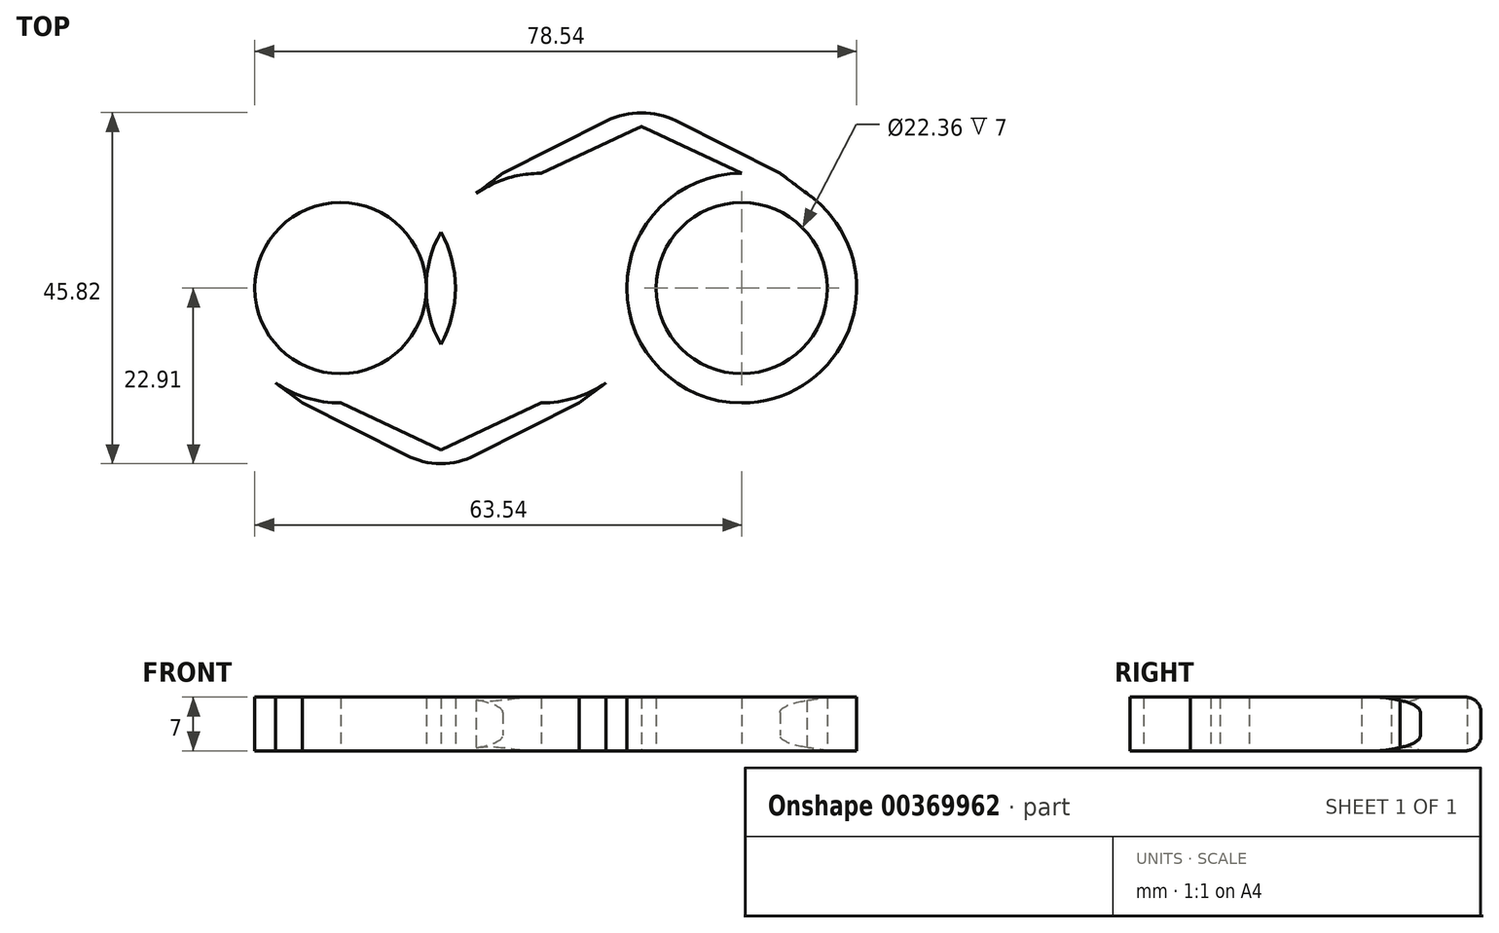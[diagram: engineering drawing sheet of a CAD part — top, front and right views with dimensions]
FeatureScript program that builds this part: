
annotation { "Feature Type Name" : "Feature", "Feature Type Description" : "" }
export const myFeature = defineFeature(function(context is Context, id is Id, definition is map)
    precondition{}
    {
        {
            var Q0;
            Q0=qCreatedBy(makeId("Top.planeOp"),FACE);
            var sketch = newSketch(context, id + "F0", { "sketchPlane" : qUnion([Q0])});
            skCircle(sketch, "E0", {"center": v(0, 0) * mm, "radius": 11.18 * mm});
            skCircle(sketch, "E1", {"center": v(0, 0) * mm, "radius": 15 * mm});
            skCircle(sketch, "E2", {"center": v(-26.18, 0) * mm, "radius": 11.18 * mm});
            skCircle(sketch, "E3", {"center": v(-26.18, 0) * mm, "radius": 15 * mm});
            skLineSegment(sketch, "E4", {"start": v(-26.18, 0) * mm, "end": v(0, 0) * mm, "construction": true});
            skLineSegment(sketch, "E5", {"start": v(-26.18, 0) * mm, "end": v(-26.18, 2) * mm, "construction": true});
            skLineSegment(sketch, "E6", {"start": v(-26.18, 0) * mm, "end": v(-26.18, -2) * mm, "construction": true});
            skLineSegment(sketch, "E7", {"start": v(0, 0) * mm, "end": v(0, 2) * mm, "construction": true});
            skLineSegment(sketch, "E8", {"start": v(0, 0) * mm, "end": v(0, -2) * mm, "construction": true});
            skLineSegment(sketch, "E9", {"start": v(-14.87, 2) * mm, "end": v(-11.3, 2) * mm});
            skLineSegment(sketch, "E10", {"start": v(-14.87, -2) * mm, "end": v(-11.3, -2) * mm});
            skLineSegment(sketch, "E11", {"start": v(-11.3, 2) * mm, "end": v(-26.18, 2) * mm, "construction": true});
            skLineSegment(sketch, "E12", {"start": v(-26.18, -2) * mm, "end": v(-11.3, -2) * mm, "construction": true});
            skLineSegment(sketch, "E13", {"start": v(-14.87, 2) * mm, "end": v(0, 2) * mm, "construction": true});
            skLineSegment(sketch, "E14", {"start": v(-14.87, -2) * mm, "end": v(0, -2) * mm, "construction": true});
            skLineSegment(sketch, "E15", {"start": v(-26.17, -2) * mm, "end": v(-26.17, -15) * mm, "construction": true});
            skLineSegment(sketch, "E16", {"start": v(0, -2) * mm, "end": v(0, -15) * mm, "construction": true});
            skLineSegment(sketch, "E17.MirrorCS", {"start": v(26.18, 0) * mm, "end": v(26.18, 2) * mm, "construction": true});
            skLineSegment(sketch, "E18.MirrorCS", {"start": v(26.18, 0) * mm, "end": v(26.18, -2) * mm, "construction": true});
            skLineSegment(sketch, "E19.MirrorCS", {"start": v(14.87, 2) * mm, "end": v(11.3, 2) * mm});
            skLineSegment(sketch, "E20.MirrorCS", {"start": v(14.87, -2) * mm, "end": v(11.3, -2) * mm});
            skLineSegment(sketch, "E21.MirrorCS", {"start": v(14.87, -2) * mm, "end": v(0, -2) * mm, "construction": true});
            skLineSegment(sketch, "E22.MirrorCS", {"start": v(26.18, -2) * mm, "end": v(26.18, -15) * mm, "construction": true});
            skCircle(sketch, "E23.MirrorC", {"center": v(26.18, 0) * mm, "radius": 15 * mm});
            skLineSegment(sketch, "E24.MirrorCS", {"start": v(26.18, 0) * mm, "end": v(0, 0) * mm, "construction": true});
            skLineSegment(sketch, "E25.MirrorCS", {"start": v(26.18, -2) * mm, "end": v(11.3, -2) * mm, "construction": true});
            skLineSegment(sketch, "E26.MirrorCS", {"start": v(11.3, 2) * mm, "end": v(26.18, 2) * mm, "construction": true});
            skCircle(sketch, "E27.MirrorC", {"center": v(26.18, 0) * mm, "radius": 11.18 * mm});
            skLineSegment(sketch, "E28.MirrorCS", {"start": v(14.87, 2) * mm, "end": v(0, 2) * mm, "construction": true});
            skLineSegment(sketch, "E29.MirrorCS", {"start": v(0, 2) * mm, "end": v(0, 15) * mm, "construction": true});
            skLineSegment(sketch, "E30.MirrorCS", {"start": v(-26.18, 2) * mm, "end": v(-11.3, 2) * mm, "construction": true});
            skLineSegment(sketch, "E31.MirrorCS", {"start": v(11.3, -2) * mm, "end": v(26.18, -2) * mm, "construction": true});
            skLineSegment(sketch, "E32.MirrorCS", {"start": v(-26.17, 2) * mm, "end": v(-26.18, 15) * mm, "construction": true});
            skLineSegment(sketch, "E33.MirrorCS", {"start": v(-11.3, -2) * mm, "end": v(-26.18, -2) * mm, "construction": true});
            skLineSegment(sketch, "E34.MirrorCS", {"start": v(26.18, 2) * mm, "end": v(11.3, 2) * mm, "construction": true});
            skLineSegment(sketch, "E35.MirrorCS", {"start": v(26.18, 2) * mm, "end": v(26.18, 15) * mm, "construction": true});
            skLineSegment(sketch, "E36", {"start": v(-26.17, -15) * mm, "end": v(0, -15) * mm, "construction": true});
            skPoint(sketch, "E37.endSnap0", {"position": v(-13.09, -2) * mm});
            skLineSegment(sketch, "E38", {"start": v(-26.17, -15) * mm, "end": v(-31.17, -15) * mm});
            skLineSegment(sketch, "E39", {"start": v(0, -15) * mm, "end": v(5, -15) * mm});
            skLineSegment(sketch, "E40", {"start": v(0, -15) * mm, "end": v(-13.09, -21.1) * mm});
            skLineSegment(sketch, "E41", {"start": v(-26.17, -15) * mm, "end": v(-13.09, -21.1) * mm});
            skLineSegment(sketch, "E42", {"start": v(-13.09, -21.1) * mm, "end": v(-13.09, -24.1) * mm});
            skLineSegment(sketch, "E43", {"start": v(-31.17, -15) * mm, "end": v(-13.09, -24.1) * mm});
            skLineSegment(sketch, "E44", {"start": v(-13.09, -24.1) * mm, "end": v(5, -15) * mm});
            skLineSegment(sketch, "E45", {"start": v(5, -15) * mm, "end": v(8.55, -12.32) * mm});
            skLineSegment(sketch, "E46", {"start": v(-31.17, -15) * mm, "end": v(-34.73, -12.32) * mm});
            skLineSegment(sketch, "E47.MirrorCS", {"start": v(-5, -15) * mm, "end": v(-8.55, -12.32) * mm});
            skLineSegment(sketch, "E48.MirrorCS", {"start": v(31.17, -15) * mm, "end": v(13.09, -24.1) * mm});
            skLineSegment(sketch, "E49.MirrorCS", {"start": v(0, -15) * mm, "end": v(13.09, -21.1) * mm});
            skLineSegment(sketch, "E50.MirrorCS", {"start": v(26.17, -15) * mm, "end": v(13.09, -21.1) * mm});
            skLineSegment(sketch, "E51.MirrorCS", {"start": v(26.17, -15) * mm, "end": v(31.17, -15) * mm});
            skLineSegment(sketch, "E52.MirrorCS", {"start": v(31.17, -15) * mm, "end": v(34.73, -12.32) * mm});
            skLineSegment(sketch, "E53.MirrorCS", {"start": v(0, -15) * mm, "end": v(-5, -15) * mm});
            skLineSegment(sketch, "E54.MirrorCS", {"start": v(13.09, -21.1) * mm, "end": v(13.09, -24.1) * mm});
            skLineSegment(sketch, "E55.MirrorCS", {"start": v(13.09, -24.1) * mm, "end": v(-5, -15) * mm});
            skLineSegment(sketch, "E56.MirrorCS", {"start": v(26.17, -15) * mm, "end": v(0, -15) * mm, "construction": true});
            skLineSegment(sketch, "E57.MirrorCS", {"start": v(0, 15) * mm, "end": v(-5, 15) * mm});
            skLineSegment(sketch, "E58.MirrorCS", {"start": v(0, 15) * mm, "end": v(5, 15) * mm});
            skLineSegment(sketch, "E59.MirrorCS", {"start": v(-26.17, 15) * mm, "end": v(-31.17, 15) * mm});
            skLineSegment(sketch, "E60.MirrorCS", {"start": v(13.09, 21.1) * mm, "end": v(13.09, 24.1) * mm});
            skLineSegment(sketch, "E61.MirrorCS", {"start": v(5, 15) * mm, "end": v(8.55, 12.32) * mm});
            skLineSegment(sketch, "E62.MirrorCS", {"start": v(-13.09, 24.1) * mm, "end": v(5, 15) * mm});
            skLineSegment(sketch, "E63.MirrorCS", {"start": v(-13.09, 21.1) * mm, "end": v(-13.09, 24.1) * mm});
            skLineSegment(sketch, "E64.MirrorCS", {"start": v(26.17, 15) * mm, "end": v(31.17, 15) * mm});
            skLineSegment(sketch, "E65.MirrorCS", {"start": v(31.17, 15) * mm, "end": v(13.09, 24.1) * mm});
            skLineSegment(sketch, "E66.MirrorCS", {"start": v(-31.17, 15) * mm, "end": v(-13.09, 24.1) * mm});
            skLineSegment(sketch, "E67.MirrorCS", {"start": v(26.17, 15) * mm, "end": v(0, 15) * mm, "construction": true});
            skLineSegment(sketch, "E68.MirrorCS", {"start": v(0, 15) * mm, "end": v(-13.09, 21.1) * mm});
            skLineSegment(sketch, "E69.MirrorCS", {"start": v(0, 15) * mm, "end": v(13.09, 21.1) * mm});
            skLineSegment(sketch, "E70.MirrorCS", {"start": v(-5, 15) * mm, "end": v(-8.55, 12.32) * mm});
            skLineSegment(sketch, "E71.MirrorCS", {"start": v(-26.17, 15) * mm, "end": v(0, 15) * mm, "construction": true});
            skLineSegment(sketch, "E72.MirrorCS", {"start": v(-26.17, 15) * mm, "end": v(-13.09, 21.1) * mm});
            skLineSegment(sketch, "E73.MirrorCS", {"start": v(26.17, 15) * mm, "end": v(13.09, 21.1) * mm});
            skLineSegment(sketch, "E74.MirrorCS", {"start": v(13.09, 24.1) * mm, "end": v(-5, 15) * mm});
            skLineSegment(sketch, "E75.MirrorCS", {"start": v(-31.17, 15) * mm, "end": v(-34.73, 12.32) * mm});
            skLineSegment(sketch, "E76.MirrorCS", {"start": v(31.17, 15) * mm, "end": v(34.73, 12.32) * mm});
            skSolve(sketch);
        }
        {
            var Q0;
            {var subQ8=sQuery(id+"F0.wireOp",EDGE,"E2");Q0=makeQuery(id+"F0.imprint","IMPRINT",FACE,{"disambiguationData":[TD([[makeQuery(id+"F0.imprint","IMPRINT",EDGE,{"derivedFrom":subQ8}),1.0]])]});}
            var Q1;
            {var subQ6=sQuery(id+"F0.wireOp",EDGE,"E27.MirrorC");Q1=makeQuery(id+"F0.imprint","IMPRINT",FACE,{"disambiguationData":[TD([[makeQuery(id+"F0.imprint","IMPRINT",EDGE,{"derivedFrom":subQ6}),-1.0]])]});}
            var Q2;
            {var subQ4=sQuery(id+"F0.wireOp",EDGE,"E3");var subQ5=makeQuery(id+"F0.imprint","INTERSECT",VERTEX,{"derivedFrom":[sQuery(id+"F0.wireOp",EDGE,"E9"),subQ4]});Q2=makeQuery(id+"F0.imprint","IMPRINT",FACE,{"disambiguationData":[TD([[makeQuery(id+"F0.imprint","IMPRINT",EDGE,{"disambiguationData":[TD([[subQ5,1.0]])],"derivedFrom":subQ4}),1.0]])]});}
            var Q3;
            {var subQ0=sQuery(id+"F0.wireOp",EDGE,"E42");Q3=makeQuery(id+"F0.imprint","IMPRINT",FACE,{"disambiguationData":[TD([[makeQuery(id+"F0.imprint","IMPRINT",EDGE,{"derivedFrom":subQ0}),1.0]])]});}
            var Q4;
            {var subQ1=sQuery(id+"F0.wireOp",EDGE,"E20.MirrorCS");Q4=makeQuery(id+"F0.imprint","IMPRINT",FACE,{"disambiguationData":[TD([[makeQuery(id+"F0.imprint","IMPRINT",EDGE,{"derivedFrom":subQ1}),-1.0]])]});}
            var Q5;
            {var subQ0=sQuery(id+"F0.wireOp",EDGE,"E10");Q5=makeQuery(id+"F0.imprint","IMPRINT",FACE,{"disambiguationData":[TD([[makeQuery(id+"F0.imprint","IMPRINT",EDGE,{"derivedFrom":subQ0}),-1.0]])]});}
            var Q6;
            {var subQ0=sQuery(id+"F0.wireOp",EDGE,"E9");Q6=makeQuery(id+"F0.imprint","IMPRINT",FACE,{"disambiguationData":[TD([[makeQuery(id+"F0.imprint","IMPRINT",EDGE,{"derivedFrom":subQ0}),1.0]])]});}
            var Q7;
            {var subQ0=sQuery(id+"F0.wireOp",EDGE,"E74.MirrorCS");var subQ1=sQuery(id+"F0.wireOp",EDGE,"E62.MirrorCS");var subQ2=makeQuery(id+"F0.imprint","INTERSECT",VERTEX,{"derivedFrom":[subQ1,subQ0]});Q7=makeQuery(id+"F0.imprint","IMPRINT",FACE,{"disambiguationData":[TD([[makeQuery(id+"F0.imprint","IMPRINT",EDGE,{"disambiguationData":[TD([[subQ2,-1.0]])],"derivedFrom":subQ1}),-1.0]])]});}
            var Q8;
            {var subQ3=sQuery(id+"F0.wireOp",EDGE,"E55.MirrorCS");var subQ5=sQuery(id+"F0.wireOp",EDGE,"E44");var subQ6=makeQuery(id+"F0.imprint","INTERSECT",VERTEX,{"derivedFrom":[subQ5,subQ3]});Q8=makeQuery(id+"F0.imprint","IMPRINT",FACE,{"disambiguationData":[TD([[makeQuery(id+"F0.imprint","IMPRINT",EDGE,{"disambiguationData":[TD([[subQ6,-1.0]])],"derivedFrom":subQ5}),1.0]])]});}
            var Q9;
            {var subQ0=sQuery(id+"F0.wireOp",EDGE,"E57.MirrorCS");Q9=makeQuery(id+"F0.imprint","IMPRINT",FACE,{"disambiguationData":[TD([[makeQuery(id+"F0.imprint","IMPRINT",EDGE,{"derivedFrom":subQ0}),-1.0]])]});}
            var Q10;
            Q10=makeQuery(id+"F0.imprint","IMPRINT",FACE,{"disambiguationData":[TD([[makeQuery(id+"F0.imprint","IMPRINT",EDGE,{"derivedFrom":sQuery(id+"F0.wireOp",EDGE,"E38")}),1.0]])]});
            var Q11;
            {var subQ4=sQuery(id+"F0.wireOp",EDGE,"E3");var subQ5=makeQuery(id+"F0.imprint","INTERSECT",VERTEX,{"derivedFrom":[sQuery(id+"F0.wireOp",EDGE,"E10"),subQ4]});Q11=makeQuery(id+"F0.imprint","IMPRINT",FACE,{"disambiguationData":[TD([[makeQuery(id+"F0.imprint","IMPRINT",EDGE,{"disambiguationData":[TD([[subQ5,1.0]])],"derivedFrom":subQ4}),1.0]])]});}
            var Q12;
            {var subQ0=sQuery(id+"F0.wireOp",EDGE,"E20.MirrorCS");Q12=makeQuery(id+"F0.imprint","IMPRINT",FACE,{"disambiguationData":[TD([[makeQuery(id+"F0.imprint","IMPRINT",EDGE,{"derivedFrom":subQ0}),1.0]])]});}
            var Q13;
            {var subQ0=sQuery(id+"F0.wireOp",EDGE,"E19.MirrorCS");Q13=makeQuery(id+"F0.imprint","IMPRINT",FACE,{"disambiguationData":[TD([[makeQuery(id+"F0.imprint","IMPRINT",EDGE,{"derivedFrom":subQ0}),-1.0]])]});}
            var Q14;
            {var subQ0=sQuery(id+"F0.wireOp",EDGE,"E60.MirrorCS");Q14=makeQuery(id+"F0.imprint","IMPRINT",FACE,{"disambiguationData":[TD([[makeQuery(id+"F0.imprint","IMPRINT",EDGE,{"derivedFrom":subQ0}),1.0]])]});}
            var Q15;
            Q15=makeQuery(id+"F0.imprint","IMPRINT",FACE,{"disambiguationData":[TD([[makeQuery(id+"F0.imprint","IMPRINT",EDGE,{"derivedFrom":sQuery(id+"F0.wireOp",EDGE,"E60.MirrorCS")}),-1.0]])]});
            var Q16;
            {var subQ4=sQuery(id+"F0.wireOp",EDGE,"E10");Q16=makeQuery(id+"F0.imprint","IMPRINT",FACE,{"disambiguationData":[TD([[makeQuery(id+"F0.imprint","IMPRINT",EDGE,{"derivedFrom":subQ4}),1.0]])]});}
            var Q17;
            {var subQ0=sQuery(id+"F0.wireOp",EDGE,"E64.MirrorCS");Q17=makeQuery(id+"F0.imprint","IMPRINT",FACE,{"disambiguationData":[TD([[makeQuery(id+"F0.imprint","IMPRINT",EDGE,{"derivedFrom":subQ0}),-1.0]])]});}
            var Q18;
            {var subQ0=sQuery(id+"F0.wireOp",EDGE,"E57.MirrorCS");Q18=makeQuery(id+"F0.imprint","IMPRINT",FACE,{"disambiguationData":[TD([[makeQuery(id+"F0.imprint","IMPRINT",EDGE,{"derivedFrom":subQ0}),1.0]])]});}
            var Q19;
            {var subQ0=sQuery(id+"F0.wireOp",EDGE,"E38");Q19=makeQuery(id+"F0.imprint","IMPRINT",FACE,{"disambiguationData":[TD([[makeQuery(id+"F0.imprint","IMPRINT",EDGE,{"derivedFrom":subQ0}),-1.0]])]});}
            var Q20;
            {var subQ0=sQuery(id+"F0.wireOp",EDGE,"E39");Q20=makeQuery(id+"F0.imprint","IMPRINT",FACE,{"disambiguationData":[TD([[makeQuery(id+"F0.imprint","IMPRINT",EDGE,{"derivedFrom":subQ0}),-1.0]])]});}
            var Q21;
            {var subQ0=sQuery(id+"F0.wireOp",EDGE,"E39");Q21=makeQuery(id+"F0.imprint","IMPRINT",FACE,{"disambiguationData":[TD([[makeQuery(id+"F0.imprint","IMPRINT",EDGE,{"derivedFrom":subQ0}),1.0]])]});}
            extrude(context, id + "F1", {"entities" : qUnion([Q0, Q1, Q2, Q3, Q4, Q5, Q6, Q7, Q8, Q9, Q10, Q11, Q12, Q13, Q14, Q15, Q16, Q17, Q18, Q19, Q20, Q21]), "depth" : 7 * mm, "offsetDistance" : 25 * mm});
        }
        {
            var Q0;
            {var subQ0=sQuery(id+"F0.wireOp",EDGE,"E1");var subQ1=sQuery(id+"F0.wireOp",EDGE,"E23.MirrorC");Q0=makeQuery(id+"F1.opExtrude","SWEPT_EDGE",EDGE,{"disambiguationData":[OSD([subQ1,subQ0]),TDD([makeQuery(id+"F0.imprint","INTERSECT",VERTEX,{"disambiguationData":[OD(0.0)],"derivedFrom":[subQ1,subQ0]})])]});}
            var Q1;
            {var subQ0=sQuery(id+"F0.wireOp",EDGE,"E1");var subQ1=sQuery(id+"F0.wireOp",EDGE,"E3");Q1=makeQuery(id+"F1.opExtrude","SWEPT_EDGE",EDGE,{"disambiguationData":[OSD([subQ1,subQ0]),TDD([makeQuery(id+"F0.imprint","INTERSECT",VERTEX,{"disambiguationData":[OD(0.0)],"derivedFrom":[subQ1,subQ0]})])]});}
            var Q2;
            {var subQ0=sQuery(id+"F0.wireOp",EDGE,"E1");var subQ1=sQuery(id+"F0.wireOp",EDGE,"E3");Q2=makeQuery(id+"F1.opExtrude","SWEPT_EDGE",EDGE,{"disambiguationData":[OSD([subQ1,subQ0]),TDD([makeQuery(id+"F0.imprint","INTERSECT",VERTEX,{"disambiguationData":[OD(1.0)],"derivedFrom":[subQ1,subQ0]})])]});}
            var Q3;
            {var subQ0=sQuery(id+"F0.wireOp",EDGE,"E1");var subQ1=sQuery(id+"F0.wireOp",EDGE,"E23.MirrorC");Q3=makeQuery(id+"F1.opExtrude","SWEPT_EDGE",EDGE,{"disambiguationData":[OSD([subQ1,subQ0]),TDD([makeQuery(id+"F0.imprint","INTERSECT",VERTEX,{"disambiguationData":[OD(1.0)],"derivedFrom":[subQ1,subQ0]})])]});}
            var Q4;
            Q4=makeQuery(id+"F1.opExtrude","SWEPT_EDGE",EDGE,{"disambiguationData":[OSD([sQuery(id+"F0.wireOp",EDGE,"1a354422-e348-461c-b15d-a984b10858901.MirrorCS"),sQuery(id+"F0.wireOp",EDGE,"1a354422-e348-461c-b15d-a984b10858902.MirrorCS"),sQuery(id+"F0.wireOp",EDGE,"1a354422-e348-461c-b15d-a984b10858904.MirrorCS")])]});
            var Q5;
            Q5=makeQuery(id+"F1.opExtrude","SWEPT_EDGE",EDGE,{"disambiguationData":[OSD([sQuery(id+"F0.wireOp",EDGE,"E37"),sQuery(id+"F0.wireOp",EDGE,"i5YcPejx-3cUs-TQMj-GmWC-BBd8XMig79w0"),sQuery(id+"F0.wireOp",EDGE,"FcY8GOIZ-YQIf-1PoK-j5Fd-vnZbnsnqqyHF")])]});
            var Q6;
            Q6=makeQuery(id+"F1.opExtrude","SWEPT_EDGE",EDGE,{"disambiguationData":[OSD([sQuery(id+"F0.wireOp",EDGE,"FcY8GOIZ-YQIf-1PoK-j5Fd-vnZbnsnqqyHF"),sQuery(id+"F0.wireOp",EDGE,"r8vJjbD3-u1k2-9U3Z-5MgG-UqVwciMb7Je2"),sQuery(id+"F0.wireOp",EDGE,"6fVAZpAK-EvBT-bxhy-TbX8-SXOpsk91fnaQ")])]});
            var Q7;
            Q7=makeQuery(id+"F1.opExtrude","SWEPT_EDGE",EDGE,{"disambiguationData":[OSD([sQuery(id+"F0.wireOp",EDGE,"1a354422-e348-461c-b15d-a984b10858901.MirrorCS"),sQuery(id+"F0.wireOp",EDGE,"1a354422-e348-461c-b15d-a984b10858908.MirrorCS"),sQuery(id+"F0.wireOp",EDGE,"1a354422-e348-461c-b15d-a984b10858909.MirrorCS")])]});
            var Q8;
            Q8=makeQuery(id+"F1.opExtrude","SWEPT_EDGE",EDGE,{"disambiguationData":[OSD([sQuery(id+"F0.wireOp",EDGE,"E42"),sQuery(id+"F0.wireOp",EDGE,"E43"),sQuery(id+"F0.wireOp",EDGE,"E44")])]});
            var Q9;
            Q9=makeQuery(id+"F1.opExtrude","SWEPT_EDGE",EDGE,{"disambiguationData":[OSD([sQuery(id+"F0.wireOp",EDGE,"E60.MirrorCS"),sQuery(id+"F0.wireOp",EDGE,"E65.MirrorCS"),sQuery(id+"F0.wireOp",EDGE,"E74.MirrorCS")])]});
            fillet(context, id + "F2", {"entities" : qUnion([Q0, Q1, Q2, Q3, Q4, Q5, Q6, Q7, Q8, Q9]), "radius" : 10 * mm, "tangentPropagation" : true, "allowEdgeOverflow" : false});
        }
        {
            var Q0;
            {var subQ0=sQuery(id+"F0.wireOp",EDGE,"E1");var subQ1=sQuery(id+"F0.wireOp",EDGE,"E3");Q0=makeQuery(id+"F2.opFillet","BLEND_EDGE",EDGE,{"blendedFrom":[makeQuery(id+"F1.opExtrude","SWEPT_EDGE",EDGE,{"disambiguationData":[OSD([subQ1,subQ0]),TDD([makeQuery(id+"F0.imprint","INTERSECT",VERTEX,{"disambiguationData":[OD(1.0)],"derivedFrom":[subQ1,subQ0]})])]}),makeQuery(id+"F1.opExtrude","CAP_FACE",FACE,{"disambiguationData":[OSD([sQuery(id+"F0.wireOp",EDGE,"E27.MirrorC"),subQ1,sQuery(id+"F0.wireOp",EDGE,"E23.MirrorC"),sQuery(id+"F0.wireOp",EDGE,"E2"),subQ0,sQuery(id+"F0.wireOp",EDGE,"E0"),sQuery(id+"F0.wireOp",EDGE,"E37"),sQuery(id+"F0.wireOp",EDGE,"i5YcPejx-3cUs-TQMj-GmWC-BBd8XMig79w0"),sQuery(id+"F0.wireOp",EDGE,"r8vJjbD3-u1k2-9U3Z-5MgG-UqVwciMb7Je2"),sQuery(id+"F0.wireOp",EDGE,"6fVAZpAK-EvBT-bxhy-TbX8-SXOpsk91fnaQ"),sQuery(id+"F0.wireOp",EDGE,"32a3a03e-3f7b-4444-bb6b-6f0b14f44c2e4.MirrorCS"),sQuery(id+"F0.wireOp",EDGE,"1a354422-e348-461c-b15d-a984b10858902.MirrorCS"),sQuery(id+"F0.wireOp",EDGE,"1a354422-e348-461c-b15d-a984b10858903.MirrorCS"),sQuery(id+"F0.wireOp",EDGE,"1a354422-e348-461c-b15d-a984b10858904.MirrorCS"),sQuery(id+"F0.wireOp",EDGE,"1a354422-e348-461c-b15d-a984b10858908.MirrorCS"),sQuery(id+"F0.wireOp",EDGE,"1a354422-e348-461c-b15d-a984b10858909.MirrorCS")])],"isStart":false})],"blendedInto":[makeQuery(id+"F1.opExtrude","CAP_FACE",FACE,{"disambiguationData":[OSD([sQuery(id+"F0.wireOp",EDGE,"E27.MirrorC"),subQ1,sQuery(id+"F0.wireOp",EDGE,"E23.MirrorC"),sQuery(id+"F0.wireOp",EDGE,"E2"),subQ0,sQuery(id+"F0.wireOp",EDGE,"E0"),sQuery(id+"F0.wireOp",EDGE,"E37"),sQuery(id+"F0.wireOp",EDGE,"i5YcPejx-3cUs-TQMj-GmWC-BBd8XMig79w0"),sQuery(id+"F0.wireOp",EDGE,"r8vJjbD3-u1k2-9U3Z-5MgG-UqVwciMb7Je2"),sQuery(id+"F0.wireOp",EDGE,"6fVAZpAK-EvBT-bxhy-TbX8-SXOpsk91fnaQ"),sQuery(id+"F0.wireOp",EDGE,"32a3a03e-3f7b-4444-bb6b-6f0b14f44c2e4.MirrorCS"),sQuery(id+"F0.wireOp",EDGE,"1a354422-e348-461c-b15d-a984b10858902.MirrorCS"),sQuery(id+"F0.wireOp",EDGE,"1a354422-e348-461c-b15d-a984b10858903.MirrorCS"),sQuery(id+"F0.wireOp",EDGE,"1a354422-e348-461c-b15d-a984b10858904.MirrorCS"),sQuery(id+"F0.wireOp",EDGE,"1a354422-e348-461c-b15d-a984b10858908.MirrorCS"),sQuery(id+"F0.wireOp",EDGE,"1a354422-e348-461c-b15d-a984b10858909.MirrorCS")])],"isStart":false})]});}
            var Q1;
            {var subQ0=sQuery(id+"F0.wireOp",EDGE,"E1");var subQ1=sQuery(id+"F0.wireOp",EDGE,"E23.MirrorC");Q1=makeQuery(id+"F2.opFillet","BLEND_EDGE",EDGE,{"blendedFrom":[makeQuery(id+"F1.opExtrude","SWEPT_EDGE",EDGE,{"disambiguationData":[OSD([subQ1,subQ0]),TDD([makeQuery(id+"F0.imprint","INTERSECT",VERTEX,{"disambiguationData":[OD(0.0)],"derivedFrom":[subQ1,subQ0]})])]}),makeQuery(id+"F1.opExtrude","CAP_FACE",FACE,{"disambiguationData":[OSD([sQuery(id+"F0.wireOp",EDGE,"E27.MirrorC"),sQuery(id+"F0.wireOp",EDGE,"E3"),subQ1,sQuery(id+"F0.wireOp",EDGE,"E2"),subQ0,sQuery(id+"F0.wireOp",EDGE,"E0"),sQuery(id+"F0.wireOp",EDGE,"E37"),sQuery(id+"F0.wireOp",EDGE,"i5YcPejx-3cUs-TQMj-GmWC-BBd8XMig79w0"),sQuery(id+"F0.wireOp",EDGE,"r8vJjbD3-u1k2-9U3Z-5MgG-UqVwciMb7Je2"),sQuery(id+"F0.wireOp",EDGE,"6fVAZpAK-EvBT-bxhy-TbX8-SXOpsk91fnaQ"),sQuery(id+"F0.wireOp",EDGE,"32a3a03e-3f7b-4444-bb6b-6f0b14f44c2e4.MirrorCS"),sQuery(id+"F0.wireOp",EDGE,"1a354422-e348-461c-b15d-a984b10858902.MirrorCS"),sQuery(id+"F0.wireOp",EDGE,"1a354422-e348-461c-b15d-a984b10858903.MirrorCS"),sQuery(id+"F0.wireOp",EDGE,"1a354422-e348-461c-b15d-a984b10858904.MirrorCS"),sQuery(id+"F0.wireOp",EDGE,"1a354422-e348-461c-b15d-a984b10858908.MirrorCS"),sQuery(id+"F0.wireOp",EDGE,"1a354422-e348-461c-b15d-a984b10858909.MirrorCS")])],"isStart":false})],"blendedInto":[makeQuery(id+"F1.opExtrude","CAP_FACE",FACE,{"disambiguationData":[OSD([sQuery(id+"F0.wireOp",EDGE,"E27.MirrorC"),sQuery(id+"F0.wireOp",EDGE,"E3"),subQ1,sQuery(id+"F0.wireOp",EDGE,"E2"),subQ0,sQuery(id+"F0.wireOp",EDGE,"E0"),sQuery(id+"F0.wireOp",EDGE,"E37"),sQuery(id+"F0.wireOp",EDGE,"i5YcPejx-3cUs-TQMj-GmWC-BBd8XMig79w0"),sQuery(id+"F0.wireOp",EDGE,"r8vJjbD3-u1k2-9U3Z-5MgG-UqVwciMb7Je2"),sQuery(id+"F0.wireOp",EDGE,"6fVAZpAK-EvBT-bxhy-TbX8-SXOpsk91fnaQ"),sQuery(id+"F0.wireOp",EDGE,"32a3a03e-3f7b-4444-bb6b-6f0b14f44c2e4.MirrorCS"),sQuery(id+"F0.wireOp",EDGE,"1a354422-e348-461c-b15d-a984b10858902.MirrorCS"),sQuery(id+"F0.wireOp",EDGE,"1a354422-e348-461c-b15d-a984b10858903.MirrorCS"),sQuery(id+"F0.wireOp",EDGE,"1a354422-e348-461c-b15d-a984b10858904.MirrorCS"),sQuery(id+"F0.wireOp",EDGE,"1a354422-e348-461c-b15d-a984b10858908.MirrorCS"),sQuery(id+"F0.wireOp",EDGE,"1a354422-e348-461c-b15d-a984b10858909.MirrorCS")])],"isStart":false})]});}
            var Q2;
            {var subQ0=sQuery(id+"F0.wireOp",EDGE,"E1");var subQ1=sQuery(id+"F0.wireOp",EDGE,"E23.MirrorC");Q2=makeQuery(id+"F2.opFillet","BLEND_EDGE",EDGE,{"blendedFrom":[makeQuery(id+"F1.opExtrude","SWEPT_EDGE",EDGE,{"disambiguationData":[OSD([subQ1,subQ0]),TDD([makeQuery(id+"F0.imprint","INTERSECT",VERTEX,{"disambiguationData":[OD(0.0)],"derivedFrom":[subQ1,subQ0]})])]}),makeQuery(id+"F1.opExtrude","CAP_FACE",FACE,{"disambiguationData":[OSD([sQuery(id+"F0.wireOp",EDGE,"E27.MirrorC"),sQuery(id+"F0.wireOp",EDGE,"E3"),subQ1,sQuery(id+"F0.wireOp",EDGE,"E2"),subQ0,sQuery(id+"F0.wireOp",EDGE,"E0"),sQuery(id+"F0.wireOp",EDGE,"E37"),sQuery(id+"F0.wireOp",EDGE,"i5YcPejx-3cUs-TQMj-GmWC-BBd8XMig79w0"),sQuery(id+"F0.wireOp",EDGE,"r8vJjbD3-u1k2-9U3Z-5MgG-UqVwciMb7Je2"),sQuery(id+"F0.wireOp",EDGE,"6fVAZpAK-EvBT-bxhy-TbX8-SXOpsk91fnaQ"),sQuery(id+"F0.wireOp",EDGE,"32a3a03e-3f7b-4444-bb6b-6f0b14f44c2e4.MirrorCS"),sQuery(id+"F0.wireOp",EDGE,"1a354422-e348-461c-b15d-a984b10858902.MirrorCS"),sQuery(id+"F0.wireOp",EDGE,"1a354422-e348-461c-b15d-a984b10858903.MirrorCS"),sQuery(id+"F0.wireOp",EDGE,"1a354422-e348-461c-b15d-a984b10858904.MirrorCS"),sQuery(id+"F0.wireOp",EDGE,"1a354422-e348-461c-b15d-a984b10858908.MirrorCS"),sQuery(id+"F0.wireOp",EDGE,"1a354422-e348-461c-b15d-a984b10858909.MirrorCS")])],"isStart":true})],"blendedInto":[makeQuery(id+"F1.opExtrude","CAP_FACE",FACE,{"disambiguationData":[OSD([sQuery(id+"F0.wireOp",EDGE,"E27.MirrorC"),sQuery(id+"F0.wireOp",EDGE,"E3"),subQ1,sQuery(id+"F0.wireOp",EDGE,"E2"),subQ0,sQuery(id+"F0.wireOp",EDGE,"E0"),sQuery(id+"F0.wireOp",EDGE,"E37"),sQuery(id+"F0.wireOp",EDGE,"i5YcPejx-3cUs-TQMj-GmWC-BBd8XMig79w0"),sQuery(id+"F0.wireOp",EDGE,"r8vJjbD3-u1k2-9U3Z-5MgG-UqVwciMb7Je2"),sQuery(id+"F0.wireOp",EDGE,"6fVAZpAK-EvBT-bxhy-TbX8-SXOpsk91fnaQ"),sQuery(id+"F0.wireOp",EDGE,"32a3a03e-3f7b-4444-bb6b-6f0b14f44c2e4.MirrorCS"),sQuery(id+"F0.wireOp",EDGE,"1a354422-e348-461c-b15d-a984b10858902.MirrorCS"),sQuery(id+"F0.wireOp",EDGE,"1a354422-e348-461c-b15d-a984b10858903.MirrorCS"),sQuery(id+"F0.wireOp",EDGE,"1a354422-e348-461c-b15d-a984b10858904.MirrorCS"),sQuery(id+"F0.wireOp",EDGE,"1a354422-e348-461c-b15d-a984b10858908.MirrorCS"),sQuery(id+"F0.wireOp",EDGE,"1a354422-e348-461c-b15d-a984b10858909.MirrorCS")])],"isStart":true})]});}
            var Q3;
            {var subQ0=sQuery(id+"F0.wireOp",EDGE,"E1");var subQ1=sQuery(id+"F0.wireOp",EDGE,"E3");Q3=makeQuery(id+"F2.opFillet","BLEND_EDGE",EDGE,{"blendedFrom":[makeQuery(id+"F1.opExtrude","SWEPT_EDGE",EDGE,{"disambiguationData":[OSD([subQ1,subQ0]),TDD([makeQuery(id+"F0.imprint","INTERSECT",VERTEX,{"disambiguationData":[OD(1.0)],"derivedFrom":[subQ1,subQ0]})])]}),makeQuery(id+"F1.opExtrude","CAP_FACE",FACE,{"disambiguationData":[OSD([sQuery(id+"F0.wireOp",EDGE,"E27.MirrorC"),subQ1,sQuery(id+"F0.wireOp",EDGE,"E23.MirrorC"),sQuery(id+"F0.wireOp",EDGE,"E2"),subQ0,sQuery(id+"F0.wireOp",EDGE,"E0"),sQuery(id+"F0.wireOp",EDGE,"E37"),sQuery(id+"F0.wireOp",EDGE,"i5YcPejx-3cUs-TQMj-GmWC-BBd8XMig79w0"),sQuery(id+"F0.wireOp",EDGE,"r8vJjbD3-u1k2-9U3Z-5MgG-UqVwciMb7Je2"),sQuery(id+"F0.wireOp",EDGE,"6fVAZpAK-EvBT-bxhy-TbX8-SXOpsk91fnaQ"),sQuery(id+"F0.wireOp",EDGE,"32a3a03e-3f7b-4444-bb6b-6f0b14f44c2e4.MirrorCS"),sQuery(id+"F0.wireOp",EDGE,"1a354422-e348-461c-b15d-a984b10858902.MirrorCS"),sQuery(id+"F0.wireOp",EDGE,"1a354422-e348-461c-b15d-a984b10858903.MirrorCS"),sQuery(id+"F0.wireOp",EDGE,"1a354422-e348-461c-b15d-a984b10858904.MirrorCS"),sQuery(id+"F0.wireOp",EDGE,"1a354422-e348-461c-b15d-a984b10858908.MirrorCS"),sQuery(id+"F0.wireOp",EDGE,"1a354422-e348-461c-b15d-a984b10858909.MirrorCS")])],"isStart":true})],"blendedInto":[makeQuery(id+"F1.opExtrude","CAP_FACE",FACE,{"disambiguationData":[OSD([sQuery(id+"F0.wireOp",EDGE,"E27.MirrorC"),subQ1,sQuery(id+"F0.wireOp",EDGE,"E23.MirrorC"),sQuery(id+"F0.wireOp",EDGE,"E2"),subQ0,sQuery(id+"F0.wireOp",EDGE,"E0"),sQuery(id+"F0.wireOp",EDGE,"E37"),sQuery(id+"F0.wireOp",EDGE,"i5YcPejx-3cUs-TQMj-GmWC-BBd8XMig79w0"),sQuery(id+"F0.wireOp",EDGE,"r8vJjbD3-u1k2-9U3Z-5MgG-UqVwciMb7Je2"),sQuery(id+"F0.wireOp",EDGE,"6fVAZpAK-EvBT-bxhy-TbX8-SXOpsk91fnaQ"),sQuery(id+"F0.wireOp",EDGE,"32a3a03e-3f7b-4444-bb6b-6f0b14f44c2e4.MirrorCS"),sQuery(id+"F0.wireOp",EDGE,"1a354422-e348-461c-b15d-a984b10858902.MirrorCS"),sQuery(id+"F0.wireOp",EDGE,"1a354422-e348-461c-b15d-a984b10858903.MirrorCS"),sQuery(id+"F0.wireOp",EDGE,"1a354422-e348-461c-b15d-a984b10858904.MirrorCS"),sQuery(id+"F0.wireOp",EDGE,"1a354422-e348-461c-b15d-a984b10858908.MirrorCS"),sQuery(id+"F0.wireOp",EDGE,"1a354422-e348-461c-b15d-a984b10858909.MirrorCS")])],"isStart":true})]});}
            var Q4;
            {var subQ0=sQuery(id+"F0.wireOp",EDGE,"E44");var subQ1=sQuery(id+"F0.wireOp",EDGE,"E43");Q4=makeQuery(id+"F2.opFillet","BLEND_EDGE",EDGE,{"blendedFrom":[makeQuery(id+"F1.opExtrude","SWEPT_EDGE",EDGE,{"disambiguationData":[OSD([sQuery(id+"F0.wireOp",EDGE,"E42"),subQ1,subQ0])]}),makeQuery(id+"F1.opExtrude","CAP_FACE",FACE,{"disambiguationData":[OSD([sQuery(id+"F0.wireOp",EDGE,"E27.MirrorC"),sQuery(id+"F0.wireOp",EDGE,"E3"),sQuery(id+"F0.wireOp",EDGE,"E23.MirrorC"),sQuery(id+"F0.wireOp",EDGE,"E2"),sQuery(id+"F0.wireOp",EDGE,"E1"),sQuery(id+"F0.wireOp",EDGE,"E0"),sQuery(id+"F0.wireOp",EDGE,"E40"),sQuery(id+"F0.wireOp",EDGE,"E41"),subQ1,subQ0,sQuery(id+"F0.wireOp",EDGE,"E45"),sQuery(id+"F0.wireOp",EDGE,"E46"),sQuery(id+"F0.wireOp",EDGE,"E65.MirrorCS"),sQuery(id+"F0.wireOp",EDGE,"E69.MirrorCS"),sQuery(id+"F0.wireOp",EDGE,"E70.MirrorCS"),sQuery(id+"F0.wireOp",EDGE,"E73.MirrorCS"),sQuery(id+"F0.wireOp",EDGE,"E74.MirrorCS"),sQuery(id+"F0.wireOp",EDGE,"E76.MirrorCS")])],"isStart":false})],"blendedInto":[makeQuery(id+"F1.opExtrude","CAP_FACE",FACE,{"disambiguationData":[OSD([sQuery(id+"F0.wireOp",EDGE,"E27.MirrorC"),sQuery(id+"F0.wireOp",EDGE,"E3"),sQuery(id+"F0.wireOp",EDGE,"E23.MirrorC"),sQuery(id+"F0.wireOp",EDGE,"E2"),sQuery(id+"F0.wireOp",EDGE,"E1"),sQuery(id+"F0.wireOp",EDGE,"E0"),sQuery(id+"F0.wireOp",EDGE,"E40"),sQuery(id+"F0.wireOp",EDGE,"E41"),subQ1,subQ0,sQuery(id+"F0.wireOp",EDGE,"E45"),sQuery(id+"F0.wireOp",EDGE,"E46"),sQuery(id+"F0.wireOp",EDGE,"E65.MirrorCS"),sQuery(id+"F0.wireOp",EDGE,"E69.MirrorCS"),sQuery(id+"F0.wireOp",EDGE,"E70.MirrorCS"),sQuery(id+"F0.wireOp",EDGE,"E73.MirrorCS"),sQuery(id+"F0.wireOp",EDGE,"E74.MirrorCS"),sQuery(id+"F0.wireOp",EDGE,"E76.MirrorCS")])],"isStart":false})]});}
            var Q5;
            {var subQ0=sQuery(id+"F0.wireOp",EDGE,"E74.MirrorCS");var subQ1=sQuery(id+"F0.wireOp",EDGE,"E65.MirrorCS");Q5=makeQuery(id+"F2.opFillet","BLEND_EDGE",EDGE,{"blendedFrom":[makeQuery(id+"F1.opExtrude","SWEPT_EDGE",EDGE,{"disambiguationData":[OSD([sQuery(id+"F0.wireOp",EDGE,"E60.MirrorCS"),subQ1,subQ0])]}),makeQuery(id+"F1.opExtrude","CAP_FACE",FACE,{"disambiguationData":[OSD([sQuery(id+"F0.wireOp",EDGE,"E27.MirrorC"),sQuery(id+"F0.wireOp",EDGE,"E3"),sQuery(id+"F0.wireOp",EDGE,"E23.MirrorC"),sQuery(id+"F0.wireOp",EDGE,"E2"),sQuery(id+"F0.wireOp",EDGE,"E1"),sQuery(id+"F0.wireOp",EDGE,"E0"),sQuery(id+"F0.wireOp",EDGE,"E40"),sQuery(id+"F0.wireOp",EDGE,"E41"),sQuery(id+"F0.wireOp",EDGE,"E43"),sQuery(id+"F0.wireOp",EDGE,"E44"),sQuery(id+"F0.wireOp",EDGE,"E45"),sQuery(id+"F0.wireOp",EDGE,"E46"),subQ1,sQuery(id+"F0.wireOp",EDGE,"E69.MirrorCS"),sQuery(id+"F0.wireOp",EDGE,"E70.MirrorCS"),sQuery(id+"F0.wireOp",EDGE,"E73.MirrorCS"),subQ0,sQuery(id+"F0.wireOp",EDGE,"E76.MirrorCS")])],"isStart":false})],"blendedInto":[makeQuery(id+"F1.opExtrude","CAP_FACE",FACE,{"disambiguationData":[OSD([sQuery(id+"F0.wireOp",EDGE,"E27.MirrorC"),sQuery(id+"F0.wireOp",EDGE,"E3"),sQuery(id+"F0.wireOp",EDGE,"E23.MirrorC"),sQuery(id+"F0.wireOp",EDGE,"E2"),sQuery(id+"F0.wireOp",EDGE,"E1"),sQuery(id+"F0.wireOp",EDGE,"E0"),sQuery(id+"F0.wireOp",EDGE,"E40"),sQuery(id+"F0.wireOp",EDGE,"E41"),sQuery(id+"F0.wireOp",EDGE,"E43"),sQuery(id+"F0.wireOp",EDGE,"E44"),sQuery(id+"F0.wireOp",EDGE,"E45"),sQuery(id+"F0.wireOp",EDGE,"E46"),subQ1,sQuery(id+"F0.wireOp",EDGE,"E69.MirrorCS"),sQuery(id+"F0.wireOp",EDGE,"E70.MirrorCS"),sQuery(id+"F0.wireOp",EDGE,"E73.MirrorCS"),subQ0,sQuery(id+"F0.wireOp",EDGE,"E76.MirrorCS")])],"isStart":false})]});}
            var Q6;
            {var subQ0=sQuery(id+"F0.wireOp",EDGE,"E74.MirrorCS");var subQ1=sQuery(id+"F0.wireOp",EDGE,"E65.MirrorCS");Q6=makeQuery(id+"F2.opFillet","BLEND_EDGE",EDGE,{"blendedFrom":[makeQuery(id+"F1.opExtrude","SWEPT_EDGE",EDGE,{"disambiguationData":[OSD([sQuery(id+"F0.wireOp",EDGE,"E60.MirrorCS"),subQ1,subQ0])]}),makeQuery(id+"F1.opExtrude","CAP_FACE",FACE,{"disambiguationData":[OSD([sQuery(id+"F0.wireOp",EDGE,"E27.MirrorC"),sQuery(id+"F0.wireOp",EDGE,"E3"),sQuery(id+"F0.wireOp",EDGE,"E23.MirrorC"),sQuery(id+"F0.wireOp",EDGE,"E2"),sQuery(id+"F0.wireOp",EDGE,"E1"),sQuery(id+"F0.wireOp",EDGE,"E0"),sQuery(id+"F0.wireOp",EDGE,"E40"),sQuery(id+"F0.wireOp",EDGE,"E41"),sQuery(id+"F0.wireOp",EDGE,"E43"),sQuery(id+"F0.wireOp",EDGE,"E44"),sQuery(id+"F0.wireOp",EDGE,"E45"),sQuery(id+"F0.wireOp",EDGE,"E46"),subQ1,sQuery(id+"F0.wireOp",EDGE,"E69.MirrorCS"),sQuery(id+"F0.wireOp",EDGE,"E70.MirrorCS"),sQuery(id+"F0.wireOp",EDGE,"E73.MirrorCS"),subQ0,sQuery(id+"F0.wireOp",EDGE,"E76.MirrorCS")])],"isStart":true})],"blendedInto":[makeQuery(id+"F1.opExtrude","CAP_FACE",FACE,{"disambiguationData":[OSD([sQuery(id+"F0.wireOp",EDGE,"E27.MirrorC"),sQuery(id+"F0.wireOp",EDGE,"E3"),sQuery(id+"F0.wireOp",EDGE,"E23.MirrorC"),sQuery(id+"F0.wireOp",EDGE,"E2"),sQuery(id+"F0.wireOp",EDGE,"E1"),sQuery(id+"F0.wireOp",EDGE,"E0"),sQuery(id+"F0.wireOp",EDGE,"E40"),sQuery(id+"F0.wireOp",EDGE,"E41"),sQuery(id+"F0.wireOp",EDGE,"E43"),sQuery(id+"F0.wireOp",EDGE,"E44"),sQuery(id+"F0.wireOp",EDGE,"E45"),sQuery(id+"F0.wireOp",EDGE,"E46"),subQ1,sQuery(id+"F0.wireOp",EDGE,"E69.MirrorCS"),sQuery(id+"F0.wireOp",EDGE,"E70.MirrorCS"),sQuery(id+"F0.wireOp",EDGE,"E73.MirrorCS"),subQ0,sQuery(id+"F0.wireOp",EDGE,"E76.MirrorCS")])],"isStart":true})]});}
            var Q7;
            {var subQ0=sQuery(id+"F0.wireOp",EDGE,"E44");var subQ1=sQuery(id+"F0.wireOp",EDGE,"E43");Q7=makeQuery(id+"F2.opFillet","BLEND_EDGE",EDGE,{"blendedFrom":[makeQuery(id+"F1.opExtrude","SWEPT_EDGE",EDGE,{"disambiguationData":[OSD([sQuery(id+"F0.wireOp",EDGE,"E42"),subQ1,subQ0])]}),makeQuery(id+"F1.opExtrude","CAP_FACE",FACE,{"disambiguationData":[OSD([sQuery(id+"F0.wireOp",EDGE,"E27.MirrorC"),sQuery(id+"F0.wireOp",EDGE,"E3"),sQuery(id+"F0.wireOp",EDGE,"E23.MirrorC"),sQuery(id+"F0.wireOp",EDGE,"E2"),sQuery(id+"F0.wireOp",EDGE,"E1"),sQuery(id+"F0.wireOp",EDGE,"E0"),sQuery(id+"F0.wireOp",EDGE,"E40"),sQuery(id+"F0.wireOp",EDGE,"E41"),subQ1,subQ0,sQuery(id+"F0.wireOp",EDGE,"E45"),sQuery(id+"F0.wireOp",EDGE,"E46"),sQuery(id+"F0.wireOp",EDGE,"E65.MirrorCS"),sQuery(id+"F0.wireOp",EDGE,"E69.MirrorCS"),sQuery(id+"F0.wireOp",EDGE,"E70.MirrorCS"),sQuery(id+"F0.wireOp",EDGE,"E73.MirrorCS"),sQuery(id+"F0.wireOp",EDGE,"E74.MirrorCS"),sQuery(id+"F0.wireOp",EDGE,"E76.MirrorCS")])],"isStart":true})],"blendedInto":[makeQuery(id+"F1.opExtrude","CAP_FACE",FACE,{"disambiguationData":[OSD([sQuery(id+"F0.wireOp",EDGE,"E27.MirrorC"),sQuery(id+"F0.wireOp",EDGE,"E3"),sQuery(id+"F0.wireOp",EDGE,"E23.MirrorC"),sQuery(id+"F0.wireOp",EDGE,"E2"),sQuery(id+"F0.wireOp",EDGE,"E1"),sQuery(id+"F0.wireOp",EDGE,"E0"),sQuery(id+"F0.wireOp",EDGE,"E40"),sQuery(id+"F0.wireOp",EDGE,"E41"),subQ1,subQ0,sQuery(id+"F0.wireOp",EDGE,"E45"),sQuery(id+"F0.wireOp",EDGE,"E46"),sQuery(id+"F0.wireOp",EDGE,"E65.MirrorCS"),sQuery(id+"F0.wireOp",EDGE,"E69.MirrorCS"),sQuery(id+"F0.wireOp",EDGE,"E70.MirrorCS"),sQuery(id+"F0.wireOp",EDGE,"E73.MirrorCS"),sQuery(id+"F0.wireOp",EDGE,"E74.MirrorCS"),sQuery(id+"F0.wireOp",EDGE,"E76.MirrorCS")])],"isStart":true})]});}
            fillet(context, id + "F3", {"entities" : qUnion([Q0, Q1, Q2, Q3, Q4, Q5, Q6, Q7]), "radius" : 2 * mm, "tangentPropagation" : true, "allowEdgeOverflow" : false});
        }
    });
